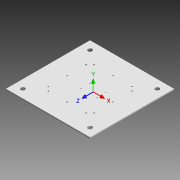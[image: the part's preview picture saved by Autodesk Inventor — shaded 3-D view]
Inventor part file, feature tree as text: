
AUTODESK INVENTOR PART (.ipt)
format: ipt  version: 2015 (Build 190159000, 159)  size: 243,200 bytes
history: native  units: in
note: dims shown in document units (in); Inventor stores cm internally (conversion verified against a paired STEP export)
features: reference x13, other x10, sketch x6, hole x3, sheet_metal_op x1
ambient origin geometry x8: Origin, YZ Plane, XZ Plane, XY Plane, X Axis, Y Axis, Z Axis, Center Point
bodies: Solid1 (feature_tree)
feature tree (33):
  sheet_metal_op  "Face1"
  other  "UCS1"
  hole  "Hole1"  [1 undecoded]
  hole  "Hole2"  [1 undecoded]
  sketch  "Sketch9"  dims[d40=0.75in]
  hole  "Hole3"  [1 undecoded]
  sketch  "Sketch1"  dims[d1=0.7874in d3=0.7874in d5=0.7874in d7=0.7874in d9=0.7874in d11=0.7874in d13=0.7874in d15=0.7874in d16=0.75in d17=0.75in d18=0.75in d19=0.75in d20=0.25in d21=0.25in d22=0.25in d23=0.25in d24=2.5681in d25=0.375in d26=1.5in d27=1.5in d28=1.5in d29=1.5in d30=1.5in d31=1.5in d32=1.5in d33=1.5in d34=90.0deg]
  other  "Plate1"
  sketch  "Sketch2"  dims[d35=45.0deg d36=90.0deg]
  sketch  "Sketch7"  dims[d37=90.0deg d38=90.0deg]
  sketch  "Sketch8"  dims[d39=0.125in]
  sketch  "Sketch10"  dims[d41=0.75in d42=5.313in d43=6.063in d44=11.376in d45=6.063in d46=0.25in d47=0.0in d48=4.2872in d49=5.9746in d50=6.063in d51=0.25in d52=8.3244in d53=4.2872in d54=0.125in d55=8.4494in d56=0.0625in d57=10.0in d58=10.0in d59=0.125in d60=8.0in d61=0.5in d62=0.5in d63=0.5in d64=0.5in d65=0.125in d66=0.0in d70=-2.5491in d71=0.0in d72=3.032in d73=0.0in d74=0.0in d75=0.0in d76=0.14in d77=0.75in d78=0.375in d79=0.25in d80=0.5635in d81=0.125in d82=0.8108in d83=0.144in d84=0.75in d85=0.279in d86=0.25in d87=0.5635in d88=0.125in d89=0.8108in d90=3.6662in d91=4.4695in d92=0.177in d93=0.328in d94=0.332in d95=0.25in d96=0.5635in d97=0.484in d98=0.8108in]
  reference  "Reference1"
  reference  "Reference2"
  reference  "Reference3"
  reference  "Reference4"
  reference  "Reference5"
  reference  "Reference6"
  reference  "Reference7"
  reference  "Reference8"
  reference  "Reference9"
  reference  "Reference10"
  reference  "Reference11"
  reference  "Reference12"
  reference  "Reference13"
  other  "Cut1"
  other  "UCS1: YZ Plane"
  other  "UCS1: XZ Plane"
  other  "UCS1: XY Plane"
  other  "UCS1: X Axis"
  other  "UCS1: Y Axis"
  other  "UCS1: Z Axis"
  other  "UCS1: Center Point"
note: 3 required parameter values undecoded (feature->parameter linkage not recoverable at this tier; creation-order binding heuristic only, values carry confidence <= 0.55)
